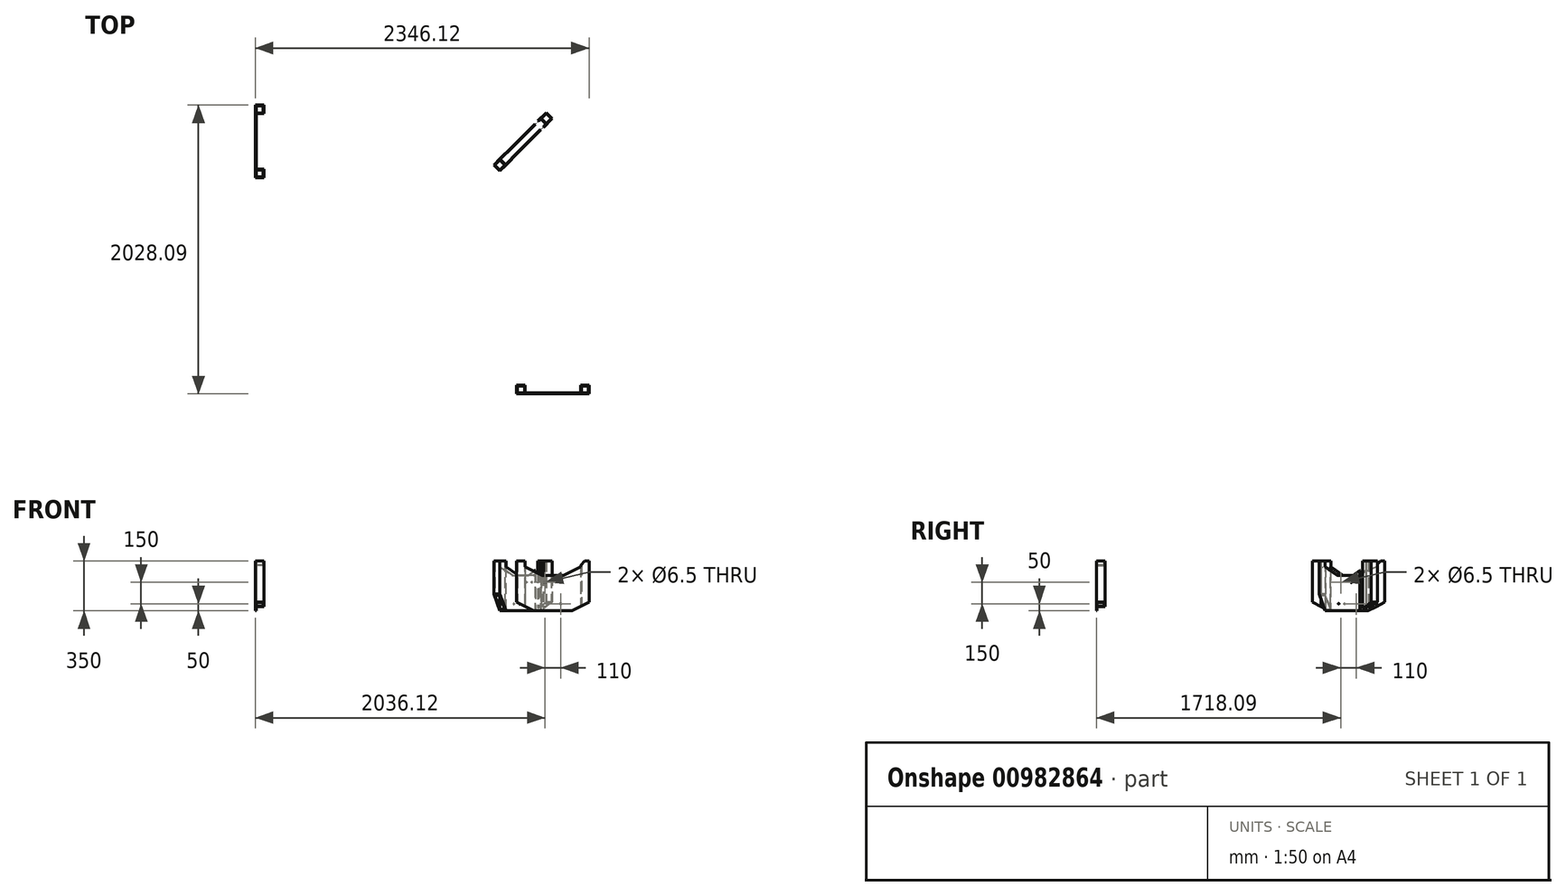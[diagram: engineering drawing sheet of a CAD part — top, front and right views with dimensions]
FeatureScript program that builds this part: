
annotation { "Feature Type Name" : "Feature", "Feature Type Description" : "" }
export const myFeature = defineFeature(function(context is Context, id is Id, definition is map)
    precondition{}
    {
        {
            var Q0;
            Q0=qCreatedBy(makeId("Top.planeOp"),FACE);
            var sketch = newSketch(context, id + "F0", { "sketchPlane" : qUnion([Q0])});
            skPoint(sketch, "E0.visualSharp", {"position": v(658.77, 766.57) * mm});
            skLineSegment(sketch, "E1.left", {"start": v(-1685.76, 286.57) * mm, "end": v(-1685.76, -13.43) * mm});
            skLineSegment(sketch, "E2.bottom", {"start": v(-1805.76, 536.57) * mm, "end": v(-1745.76, 536.57) * mm});
            skLineSegment(sketch, "E2.top", {"start": v(-1805.76, -163.43) * mm, "end": v(-1745.76, -163.43) * mm});
            skLineSegment(sketch, "E2.left", {"start": v(-1805.76, 536.57) * mm, "end": v(-1805.76, -163.43) * mm});
            skLineSegment(sketch, "E2.right", {"start": v(-1745.76, 536.57) * mm, "end": v(-1745.76, -163.43) * mm});
            skLineSegment(sketch, "E3", {"start": v(-1800.76, -163.43) * mm, "end": v(-1800.76, 536.57) * mm});
            skLineSegment(sketch, "E4", {"start": v(-1750.76, 536.57) * mm, "end": v(-1750.76, -163.43) * mm});
            skLineSegment(sketch, "E5.bottom", {"start": v(-64.64, -1586.52) * mm, "end": v(635.36, -1586.52) * mm});
            skLineSegment(sketch, "E5.top", {"start": v(-64.64, -1526.52) * mm, "end": v(635.36, -1526.52) * mm});
            skLineSegment(sketch, "E5.left", {"start": v(-64.64, -1586.52) * mm, "end": v(-64.64, -1526.52) * mm});
            skLineSegment(sketch, "E5.right", {"start": v(635.36, -1586.52) * mm, "end": v(635.36, -1526.52) * mm});
            skLineSegment(sketch, "E6", {"start": v(-64.64, -1531.52) * mm, "end": v(635.36, -1531.52) * mm});
            skLineSegment(sketch, "E7", {"start": v(635.36, -1581.52) * mm, "end": v(-64.64, -1581.52) * mm});
            skLineSegment(sketch, "E8.bottom", {"start": v(-1735.76, 581.57) * mm, "end": v(-1685.76, 581.57) * mm});
            skLineSegment(sketch, "E8.top", {"start": v(-1735.76, -208.43) * mm, "end": v(-1685.76, -208.43) * mm});
            skLineSegment(sketch, "E8.left", {"start": v(-1735.76, 581.57) * mm, "end": v(-1735.76, -208.43) * mm});
            skLineSegment(sketch, "E8.right", {"start": v(-1685.76, 581.57) * mm, "end": v(-1685.76, -208.43) * mm});
            skLineSegment(sketch, "E9.bottom", {"start": v(-1685.76, -208.43) * mm, "end": v(-460.76, -208.43) * mm});
            skLineSegment(sketch, "E9.top", {"start": v(-1685.76, -183.43) * mm, "end": v(-460.76, -183.43) * mm});
            skLineSegment(sketch, "E9.left", {"start": v(-1685.76, -208.43) * mm, "end": v(-1685.76, -183.43) * mm});
            skLineSegment(sketch, "E9.right", {"start": v(-460.76, -208.43) * mm, "end": v(-460.76, -183.43) * mm});
            skLineSegment(sketch, "E10.bottom", {"start": v(-1685.76, 581.57) * mm, "end": v(-460.76, 581.57) * mm});
            skLineSegment(sketch, "E10.top", {"start": v(-1685.76, 491.57) * mm, "end": v(-460.76, 491.57) * mm});
            skLineSegment(sketch, "E10.left", {"start": v(-1685.76, 581.57) * mm, "end": v(-1685.76, 491.57) * mm});
            skLineSegment(sketch, "E10.right", {"start": v(-460.76, 581.57) * mm, "end": v(-460.76, 491.57) * mm});
            skLineSegment(sketch, "E11", {"start": v(-341.23, -28.43) * mm, "end": v(-136.23, -28.43) * mm});
            skLineSegment(sketch, "E12", {"start": v(-136.23, -28.43) * mm, "end": v(-136.23, -233.43) * mm});
            skLineSegment(sketch, "E13", {"start": v(-341.23, -3.43) * mm, "end": v(-111.23, -3.43) * mm});
            skLineSegment(sketch, "E14", {"start": v(-111.23, -3.43) * mm, "end": v(-111.23, -233.43) * mm});
            skLineSegment(sketch, "E15.bottom", {"start": v(-520.76, 491.57) * mm, "end": v(-545.76, 491.57) * mm});
            skLineSegment(sketch, "E15.top", {"start": v(-520.76, -183.43) * mm, "end": v(-545.76, -183.43) * mm});
            skLineSegment(sketch, "E15.left", {"start": v(-520.76, 491.57) * mm, "end": v(-520.76, -183.43) * mm});
            skLineSegment(sketch, "E15.right", {"start": v(-545.76, 491.57) * mm, "end": v(-545.76, -183.43) * mm});
            skLineSegment(sketch, "E16.bottom", {"start": v(-291.23, -3.43) * mm, "end": v(-266.23, -3.43) * mm});
            skLineSegment(sketch, "E17.left", {"start": v(-111.23, -158.43) * mm, "end": v(-111.23, -183.43) * mm});
            skLineSegment(sketch, "E18", {"start": v(-109.64, -1491.52) * mm, "end": v(-109.64, -1516.52) * mm});
            skLineSegment(sketch, "E19", {"start": v(-109.64, -1516.52) * mm, "end": v(680.36, -1516.52) * mm});
            skLineSegment(sketch, "E20", {"start": v(680.36, -1516.52) * mm, "end": v(680.36, -1491.52) * mm});
            skLineSegment(sketch, "E21.top", {"start": v(-109.64, -391.52) * mm, "end": v(-84.64, -391.52) * mm});
            skLineSegment(sketch, "E21.left", {"start": v(-109.64, -1491.52) * mm, "end": v(-109.64, -391.52) * mm});
            skLineSegment(sketch, "E21.right", {"start": v(-84.64, -1491.52) * mm, "end": v(-84.64, -391.52) * mm});
            skLineSegment(sketch, "E22.top", {"start": v(680.36, -391.52) * mm, "end": v(590.36, -391.52) * mm});
            skLineSegment(sketch, "E22.left", {"start": v(680.36, -1491.52) * mm, "end": v(680.36, -391.52) * mm});
            skLineSegment(sketch, "E22.right", {"start": v(590.36, -1491.52) * mm, "end": v(590.36, -391.52) * mm});
            skLineSegment(sketch, "E23.bottom", {"start": v(-84.64, -441.52) * mm, "end": v(590.36, -441.52) * mm});
            skLineSegment(sketch, "E23.top", {"start": v(-84.64, -466.52) * mm, "end": v(590.36, -466.52) * mm});
            skLineSegment(sketch, "E23.left", {"start": v(-84.64, -441.52) * mm, "end": v(-84.64, -466.52) * mm});
            skLineSegment(sketch, "E23.right", {"start": v(590.36, -441.52) * mm, "end": v(590.36, -466.52) * mm});
            skLineSegment(sketch, "E24.top", {"start": v(-1745.76, 11.57) * mm, "end": v(-1735.76, 11.57) * mm});
            skLineSegment(sketch, "E24.left", {"start": v(-1745.76, 49.07) * mm, "end": v(-1745.76, 11.57) * mm});
            skLineSegment(sketch, "E24.right", {"start": v(-1735.76, 49.07) * mm, "end": v(-1735.76, 11.57) * mm});
            skLineSegment(sketch, "E25.left", {"start": v(-1745.76, 349.07) * mm, "end": v(-1745.76, 324.07) * mm});
            skLineSegment(sketch, "E25.right", {"start": v(-1735.76, 349.07) * mm, "end": v(-1735.76, 324.07) * mm});
            skLineSegment(sketch, "E26.bottom", {"start": v(110.36, -1526.52) * mm, "end": v(160.36, -1526.52) * mm});
            skLineSegment(sketch, "E26.top", {"start": v(110.36, -1516.52) * mm, "end": v(160.36, -1516.52) * mm});
            skLineSegment(sketch, "E26.left", {"start": v(110.36, -1526.52) * mm, "end": v(110.36, -1516.52) * mm});
            skLineSegment(sketch, "E26.right", {"start": v(160.36, -1526.52) * mm, "end": v(160.36, -1516.52) * mm});
            skLineSegment(sketch, "E27.bottom", {"start": v(410.36, -1526.52) * mm, "end": v(460.36, -1526.52) * mm});
            skLineSegment(sketch, "E27.top", {"start": v(410.36, -1516.52) * mm, "end": v(460.36, -1516.52) * mm});
            skLineSegment(sketch, "E27.left", {"start": v(410.36, -1526.52) * mm, "end": v(410.36, -1516.52) * mm});
            skLineSegment(sketch, "E27.right", {"start": v(460.36, -1526.52) * mm, "end": v(460.36, -1516.52) * mm});
            skLineSegment(sketch, "E28", {"start": v(-128.9, 14.25) * mm, "end": v(220.91, 364.07) * mm});
            skLineSegment(sketch, "E29", {"start": v(-93.55, -21.1) * mm, "end": v(256.27, 328.72) * mm});
            skLineSegment(sketch, "E30", {"start": v(256.27, 328.72) * mm, "end": v(273.95, 346.4) * mm});
            skLineSegment(sketch, "E31", {"start": v(220.91, 364.07) * mm, "end": v(238.6, 381.75) * mm});
            skLineSegment(sketch, "E32", {"start": v(238.6, 381.75) * mm, "end": v(273.95, 417.1) * mm});
            skLineSegment(sketch, "E33", {"start": v(309.3, 381.75) * mm, "end": v(273.95, 346.4) * mm});
            skLineSegment(sketch, "E34", {"start": v(309.3, 381.75) * mm, "end": v(380.01, 452.46) * mm});
            skLineSegment(sketch, "E35", {"start": v(380.01, 452.46) * mm, "end": v(344.66, 487.81) * mm});
            skLineSegment(sketch, "E36", {"start": v(344.66, 487.81) * mm, "end": v(273.95, 417.1) * mm});
            skLineSegment(sketch, "E37", {"start": v(380.01, 452.46) * mm, "end": v(383.55, 448.92) * mm});
            skLineSegment(sketch, "E38", {"start": v(383.55, 448.92) * mm, "end": v(-111.23, -45.86) * mm});
            skLineSegment(sketch, "E39", {"start": v(-93.55, -21.1) * mm, "end": v(-111.23, -38.78) * mm});
            skLineSegment(sketch, "E40", {"start": v(-128.9, 14.25) * mm, "end": v(-146.59, -3.43) * mm});
            skLineSegment(sketch, "E41", {"start": v(344.66, 487.81) * mm, "end": v(341.12, 491.35) * mm});
            skLineSegment(sketch, "E42", {"start": v(341.12, 491.35) * mm, "end": v(-153.66, -3.43) * mm});
            skLineSegment(sketch, "E43", {"start": v(247.43, 390.59) * mm, "end": v(282.78, 355.23) * mm});
            skLineSegment(sketch, "E44", {"start": v(-341.23, -28.43) * mm, "end": v(-341.23, -3.43) * mm});
            skLineSegment(sketch, "E45", {"start": v(-136.23, -233.43) * mm, "end": v(-111.23, -233.43) * mm});
            skLineSegment(sketch, "E46", {"start": v(-1745.76, 61.57) * mm, "end": v(-1735.76, 61.57) * mm});
            skLineSegment(sketch, "E47", {"start": v(-1745.76, 361.57) * mm, "end": v(-1735.76, 361.57) * mm});
            skLineSegment(sketch, "E48", {"start": v(-1745.76, 311.57) * mm, "end": v(-1735.76, 311.57) * mm});
            skLineSegment(sketch, "E49", {"start": v(590.36, -391.52) * mm, "end": v(-84.64, -391.52) * mm});
            skLineSegment(sketch, "E50", {"start": v(-111.23, -233.43) * mm, "end": v(603.77, -233.43) * mm});
            skLineSegment(sketch, "E51", {"start": v(-341.23, -3.43) * mm, "end": v(-341.23, 711.57) * mm});
            skLineSegment(sketch, "E52", {"start": v(-460.76, 491.57) * mm, "end": v(-460.76, -183.43) * mm});
            skLineSegment(sketch, "E53", {"start": v(-1260.76, -208.43) * mm, "end": v(-1260.76, 581.57) * mm});
            skLineSegment(sketch, "E54", {"start": v(-1235.76, 581.57) * mm, "end": v(-1235.76, -208.43) * mm});
            skLineSegment(sketch, "E55", {"start": v(-109.64, -1016.52) * mm, "end": v(680.36, -1016.52) * mm});
            skLineSegment(sketch, "E56", {"start": v(-109.64, -1041.52) * mm, "end": v(680.36, -1041.52) * mm});
            skLineSegment(sketch, "E57", {"start": v(-341.23, 711.57) * mm, "end": v(-341.23, 761.57) * mm});
            skLineSegment(sketch, "E58", {"start": v(603.77, -233.43) * mm, "end": v(653.77, -233.43) * mm});
            skLineSegment(sketch, "E59", {"start": v(282.78, 355.23) * mm, "end": v(653.77, -15.75) * mm});
            skLineSegment(sketch, "E60", {"start": v(653.77, -233.43) * mm, "end": v(653.77, -15.75) * mm});
            skLineSegment(sketch, "E61", {"start": v(247.43, 390.59) * mm, "end": v(-123.55, 761.57) * mm});
            skLineSegment(sketch, "E62", {"start": v(-341.23, 761.57) * mm, "end": v(-123.55, 761.57) * mm});
            skLineSegment(sketch, "E63", {"start": v(-111.23, -158.43) * mm, "end": v(603.77, -158.43) * mm});
            skLineSegment(sketch, "E64", {"start": v(-111.23, -183.43) * mm, "end": v(603.77, -183.43) * mm});
            skLineSegment(sketch, "E65", {"start": v(-291.23, -3.43) * mm, "end": v(-291.23, 711.57) * mm});
            skLineSegment(sketch, "E66", {"start": v(-266.23, -3.43) * mm, "end": v(-266.23, 711.57) * mm});
            skLineSegment(sketch, "E67.bottom", {"start": v(-341.23, 761.57) * mm, "end": v(-391.23, 761.57) * mm});
            skLineSegment(sketch, "E67.left", {"start": v(-341.23, 761.57) * mm, "end": v(-341.23, 711.57) * mm});
            skLineSegment(sketch, "E68.bottom", {"start": v(-341.23, -3.43) * mm, "end": v(-391.23, -3.43) * mm});
            skLineSegment(sketch, "E68.top", {"start": v(-341.23, -28.43) * mm, "end": v(-391.23, -28.43) * mm});
            skLineSegment(sketch, "E68.left", {"start": v(-341.23, -3.43) * mm, "end": v(-341.23, -28.43) * mm});
            skLineSegment(sketch, "E68.right", {"start": v(-391.23, -3.43) * mm, "end": v(-391.23, -28.43) * mm});
            skLineSegment(sketch, "E69.bottom", {"start": v(-111.23, -233.43) * mm, "end": v(-136.23, -233.43) * mm});
            skLineSegment(sketch, "E69.top", {"start": v(-111.23, -283.43) * mm, "end": v(-136.23, -283.43) * mm});
            skLineSegment(sketch, "E69.left", {"start": v(-111.23, -233.43) * mm, "end": v(-111.23, -283.43) * mm});
            skLineSegment(sketch, "E69.right", {"start": v(-136.23, -233.43) * mm, "end": v(-136.23, -283.43) * mm});
            skLineSegment(sketch, "E70.right", {"start": v(653.77, -233.43) * mm, "end": v(653.77, -283.43) * mm});
            skLineSegment(sketch, "E71", {"start": v(-1800.76, -13.43) * mm, "end": v(-1750.76, -13.43) * mm});
            skLineSegment(sketch, "E72", {"start": v(-1800.76, -63.43) * mm, "end": v(-1750.76, -63.43) * mm});
            skLineSegment(sketch, "E73.bottom", {"start": v(-1795.76, -18.43) * mm, "end": v(-1755.76, -18.43) * mm});
            skLineSegment(sketch, "E73.top", {"start": v(-1795.76, -58.43) * mm, "end": v(-1755.76, -58.43) * mm});
            skLineSegment(sketch, "E73.left", {"start": v(-1795.76, -18.43) * mm, "end": v(-1795.76, -58.43) * mm});
            skLineSegment(sketch, "E73.right", {"start": v(-1755.76, -18.43) * mm, "end": v(-1755.76, -58.43) * mm});
            skLineSegment(sketch, "E74", {"start": v(35.36, -1581.52) * mm, "end": v(35.36, -1531.52) * mm});
            skLineSegment(sketch, "E75", {"start": v(85.36, -1581.52) * mm, "end": v(85.36, -1531.52) * mm});
            skLineSegment(sketch, "E76.bottom", {"start": v(40.36, -1536.52) * mm, "end": v(80.36, -1536.52) * mm});
            skLineSegment(sketch, "E76.top", {"start": v(40.36, -1576.52) * mm, "end": v(80.36, -1576.52) * mm});
            skLineSegment(sketch, "E76.left", {"start": v(40.36, -1536.52) * mm, "end": v(40.36, -1576.52) * mm});
            skLineSegment(sketch, "E76.right", {"start": v(80.36, -1536.52) * mm, "end": v(80.36, -1576.52) * mm});
            skLineSegment(sketch, "E77", {"start": v(238.6, 311.04) * mm, "end": v(203.24, 346.4) * mm});
            skLineSegment(sketch, "E78", {"start": v(273.95, 346.4) * mm, "end": v(238.6, 381.75) * mm});
            skLineSegment(sketch, "E79", {"start": v(210.34, 346.36) * mm, "end": v(238.62, 374.65) * mm});
            skLineSegment(sketch, "E80", {"start": v(238.62, 374.65) * mm, "end": v(266.9, 346.36) * mm});
            skLineSegment(sketch, "E81", {"start": v(266.9, 346.36) * mm, "end": v(238.62, 318.08) * mm});
            skLineSegment(sketch, "E82", {"start": v(238.62, 318.08) * mm, "end": v(210.34, 346.36) * mm});
            skLineSegment(sketch, "E83", {"start": v(-109.64, -1466.52) * mm, "end": v(680.36, -1466.52) * mm});
            skLineSegment(sketch, "E84", {"start": v(-1685.76, 486.57) * mm, "end": v(-460.76, 486.57) * mm});
            skLineSegment(sketch, "E85", {"start": v(-460.76, 581.57) * mm, "end": v(-460.76, 586.57) * mm});
            skLineSegment(sketch, "E86", {"start": v(-1735.76, 581.57) * mm, "end": v(-1735.76, 586.57) * mm});
            skLineSegment(sketch, "E87", {"start": v(-1735.76, 586.57) * mm, "end": v(-460.76, 586.57) * mm});
            skLineSegment(sketch, "E88", {"start": v(-1685.76, 581.57) * mm, "end": v(-1685.76, 586.57) * mm});
            skLineSegment(sketch, "E89", {"start": v(680.36, -391.52) * mm, "end": v(685.36, -391.52) * mm});
            skLineSegment(sketch, "E90", {"start": v(680.36, -1516.52) * mm, "end": v(685.36, -1516.52) * mm});
            skLineSegment(sketch, "E91", {"start": v(680.36, -1466.52) * mm, "end": v(685.36, -1466.52) * mm});
            skLineSegment(sketch, "E92", {"start": v(685.36, -1516.52) * mm, "end": v(685.36, -391.52) * mm});
            skLineSegment(sketch, "E93", {"start": v(585.36, -391.52) * mm, "end": v(585.36, -1466.52) * mm});
            skLineSegment(sketch, "E94.bottom", {"start": v(-1217.06, 852.71) * mm, "end": v(-592.06, 852.71) * mm});
            skLineSegment(sketch, "E94.top", {"start": v(-1217.06, 752.71) * mm, "end": v(-592.06, 752.71) * mm});
            skLineSegment(sketch, "E94.left", {"start": v(-1217.06, 852.71) * mm, "end": v(-1217.06, 752.71) * mm});
            skLineSegment(sketch, "E94.right", {"start": v(-592.06, 852.71) * mm, "end": v(-592.06, 752.71) * mm});
            skLineSegment(sketch, "E95.bottom", {"start": v(943.97, -569.98) * mm, "end": v(1043.97, -569.98) * mm});
            skLineSegment(sketch, "E95.top", {"start": v(943.97, -1344.98) * mm, "end": v(1043.97, -1344.98) * mm});
            skLineSegment(sketch, "E95.left", {"start": v(943.97, -569.98) * mm, "end": v(943.97, -1344.98) * mm});
            skLineSegment(sketch, "E95.right", {"start": v(1043.97, -569.98) * mm, "end": v(1043.97, -1344.98) * mm});
            skLineSegment(sketch, "E96", {"start": v(653.77, -283.43) * mm, "end": v(658.77, -283.43) * mm});
            skLineSegment(sketch, "E97", {"start": v(286.32, 351.7) * mm, "end": v(289.86, 355.23) * mm});
            skLineSegment(sketch, "E98", {"start": v(289.86, 355.23) * mm, "end": v(658.77, -13.68) * mm});
            skLineSegment(sketch, "E99", {"start": v(658.77, -13.68) * mm, "end": v(658.77, -283.43) * mm});
            skLineSegment(sketch, "E100", {"start": v(-391.23, 761.57) * mm, "end": v(-391.23, 766.57) * mm});
            skLineSegment(sketch, "E101", {"start": v(-391.23, 766.57) * mm, "end": v(-121.48, 766.57) * mm});
            skLineSegment(sketch, "E102", {"start": v(-121.48, 766.57) * mm, "end": v(289.86, 355.23) * mm});
            skLineSegment(sketch, "E103", {"start": v(-391.23, 761.57) * mm, "end": v(-391.23, 671.57) * mm});
            skLineSegment(sketch, "E104", {"start": v(-391.23, 671.57) * mm, "end": v(-391.23, 666.57) * mm});
            skLineSegment(sketch, "E105", {"start": v(653.77, -283.43) * mm, "end": v(563.77, -283.43) * mm});
            skLineSegment(sketch, "E106", {"start": v(563.77, -283.43) * mm, "end": v(558.77, -283.43) * mm});
            skLineSegment(sketch, "E107", {"start": v(286.32, 351.7) * mm, "end": v(222.68, 288.06) * mm});
            skLineSegment(sketch, "E108", {"start": v(563.77, -283.43) * mm, "end": v(563.77, -53.03) * mm});
            skLineSegment(sketch, "E109", {"start": v(-391.23, 671.57) * mm, "end": v(-160.83, 671.57) * mm});
            skLineSegment(sketch, "E110", {"start": v(-160.83, 671.57) * mm, "end": v(563.77, -53.03) * mm});
            skLineSegment(sketch, "E111", {"start": v(180.25, 330.48) * mm, "end": v(176.72, 326.95) * mm});
            skLineSegment(sketch, "E112", {"start": v(176.72, 326.95) * mm, "end": v(-162.9, 666.57) * mm});
            skLineSegment(sketch, "E113", {"start": v(-162.9, 666.57) * mm, "end": v(-391.23, 666.57) * mm});
            skLineSegment(sketch, "E114", {"start": v(176.72, 326.95) * mm, "end": v(558.77, -55.1) * mm});
            skLineSegment(sketch, "E115", {"start": v(558.77, -55.1) * mm, "end": v(558.77, -283.43) * mm});
            skLineSegment(sketch, "E116", {"start": v(466.78, 1211.56) * mm, "end": v(466.78, 1216.56) * mm});
            skLineSegment(sketch, "E117", {"start": v(466.78, 1216.56) * mm, "end": v(736.53, 1216.56) * mm});
            skLineSegment(sketch, "E118", {"start": v(466.78, 1211.56) * mm, "end": v(466.78, 1121.56) * mm});
            skLineSegment(sketch, "E119", {"start": v(466.78, 1121.56) * mm, "end": v(466.78, 1116.56) * mm});
            skLineSegment(sketch, "E120", {"start": v(1034.73, 776.93) * mm, "end": v(695.11, 1116.56) * mm});
            skLineSegment(sketch, "E121", {"start": v(695.11, 1116.56) * mm, "end": v(466.78, 1116.56) * mm});
            skLineSegment(sketch, "E122", {"start": v(736.53, 1216.56) * mm, "end": v(1105.44, 847.64) * mm});
            skLineSegment(sketch, "E123", {"start": v(1034.73, 776.93) * mm, "end": v(1105.44, 847.64) * mm});
            skLineSegment(sketch, "E124", {"start": v(1556.93, 75.78) * mm, "end": v(1561.93, 75.78) * mm});
            skLineSegment(sketch, "E125", {"start": v(1193.02, 714.44) * mm, "end": v(1561.93, 345.53) * mm});
            skLineSegment(sketch, "E126", {"start": v(1561.93, 345.53) * mm, "end": v(1561.93, 75.78) * mm});
            skLineSegment(sketch, "E127", {"start": v(1556.93, 75.78) * mm, "end": v(1466.93, 75.78) * mm});
            skLineSegment(sketch, "E128", {"start": v(1466.93, 75.78) * mm, "end": v(1461.93, 75.78) * mm});
            skLineSegment(sketch, "E129", {"start": v(1461.93, 304.1) * mm, "end": v(1461.93, 75.78) * mm});
            skLineSegment(sketch, "E130", {"start": v(1461.93, 304.1) * mm, "end": v(1122.3, 643.73) * mm});
            skLineSegment(sketch, "E131", {"start": v(1193.02, 714.44) * mm, "end": v(1122.3, 643.73) * mm});
            skLineSegment(sketch, "E132", {"start": v(653.77, -15.75) * mm, "end": v(658.77, -13.68) * mm});
            skLineSegment(sketch, "E133", {"start": v(-123.55, 761.57) * mm, "end": v(-121.48, 766.57) * mm});
            skLineSegment(sketch, "E134", {"start": v(-311.2, 1156.99) * mm, "end": v(-93.53, 1156.99) * mm});
            skLineSegment(sketch, "E135.bottom", {"start": v(-311.2, 1156.99) * mm, "end": v(-361.2, 1156.99) * mm});
            skLineSegment(sketch, "E136", {"start": v(-361.2, 1156.99) * mm, "end": v(-361.2, 1161.99) * mm});
            skLineSegment(sketch, "E137", {"start": v(-361.2, 1161.99) * mm, "end": v(-91.46, 1161.99) * mm});
            skLineSegment(sketch, "E138", {"start": v(-93.53, 1156.99) * mm, "end": v(-91.46, 1161.99) * mm});
            skLineSegment(sketch, "E139", {"start": v(155.13, 973.03) * mm, "end": v(157.2, 978.03) * mm});
            skLineSegment(sketch, "E140", {"start": v(155.13, 973.03) * mm, "end": v(522.58, 605.58) * mm});
            skLineSegment(sketch, "E141", {"start": v(157.2, 978.03) * mm, "end": v(526.12, 609.11) * mm});
            skLineSegment(sketch, "E142", {"start": v(526.12, 609.11) * mm, "end": v(522.58, 605.58) * mm});
            skLineSegment(sketch, "E143", {"start": v(800.2, -243.65) * mm, "end": v(800.2, -25.98) * mm});
            skLineSegment(sketch, "E144.right", {"start": v(800.2, -243.65) * mm, "end": v(800.2, -293.65) * mm});
            skLineSegment(sketch, "E145", {"start": v(800.2, -293.65) * mm, "end": v(805.2, -293.65) * mm});
            skLineSegment(sketch, "E146", {"start": v(805.2, -23.9) * mm, "end": v(805.2, -293.65) * mm});
            skLineSegment(sketch, "E147", {"start": v(800.2, -25.98) * mm, "end": v(805.2, -23.9) * mm});
            skLineSegment(sketch, "E148", {"start": v(587.67, 634.51) * mm, "end": v(956.58, 265.6) * mm});
            skLineSegment(sketch, "E149", {"start": v(951.58, 263.53) * mm, "end": v(956.58, 265.6) * mm});
            skLineSegment(sketch, "E150", {"start": v(587.67, 634.51) * mm, "end": v(584.13, 630.98) * mm});
            skLineSegment(sketch, "E151", {"start": v(584.13, 630.98) * mm, "end": v(951.58, 263.53) * mm});
            skLineSegment(sketch, "E152.bottom", {"start": v(1162.31, -284.11) * mm, "end": v(1167.31, -284.11) * mm});
            skLineSegment(sketch, "E152.top", {"start": v(1162.31, -1359.11) * mm, "end": v(1167.31, -1359.11) * mm});
            skLineSegment(sketch, "E152.left", {"start": v(1162.31, -284.11) * mm, "end": v(1162.31, -1359.11) * mm});
            skLineSegment(sketch, "E152.right", {"start": v(1167.31, -284.11) * mm, "end": v(1167.31, -1359.11) * mm});
            skLineSegment(sketch, "E153.bottom", {"start": v(-1710.19, 1266.2) * mm, "end": v(-485.19, 1266.2) * mm});
            skLineSegment(sketch, "E153.top", {"start": v(-1710.19, 1261.2) * mm, "end": v(-485.19, 1261.2) * mm});
            skLineSegment(sketch, "E153.left", {"start": v(-1710.19, 1266.2) * mm, "end": v(-1710.19, 1261.2) * mm});
            skLineSegment(sketch, "E153.right", {"start": v(-485.19, 1266.2) * mm, "end": v(-485.19, 1261.2) * mm});
            skLineSegment(sketch, "E154", {"start": v(-1235.76, 461.57) * mm, "end": v(-460.76, 461.57) * mm});
            skLineSegment(sketch, "E155", {"start": v(560.36, -1016.52) * mm, "end": v(560.36, -391.52) * mm});
            skLineSegment(sketch, "E156", {"start": v(558.77, -283.43) * mm, "end": v(533.77, -283.43) * mm});
            skLineSegment(sketch, "E157", {"start": v(-391.23, 666.57) * mm, "end": v(-391.23, 641.57) * mm});
            skLineSegment(sketch, "E158", {"start": v(176.72, 326.95) * mm, "end": v(159.04, 309.27) * mm});
            skLineSegment(sketch, "E159", {"start": v(159.04, 309.27) * mm, "end": v(-173.26, 641.57) * mm});
            skLineSegment(sketch, "E160", {"start": v(219.15, 284.52) * mm, "end": v(201.47, 266.84) * mm});
            skLineSegment(sketch, "E161", {"start": v(201.47, 266.84) * mm, "end": v(159.04, 309.27) * mm});
            skLineSegment(sketch, "E162", {"start": v(201.47, 266.84) * mm, "end": v(533.77, -65.46) * mm});
            skLineSegment(sketch, "E163", {"start": v(-391.23, 641.57) * mm, "end": v(-173.26, 641.57) * mm});
            skLineSegment(sketch, "E164", {"start": v(533.77, -65.46) * mm, "end": v(533.77, -283.43) * mm});
            skLineSegment(sketch, "E165.bottom", {"start": v(-520.76, 41.57) * mm, "end": v(-460.76, 41.57) * mm});
            skLineSegment(sketch, "E165.top", {"start": v(-520.76, 16.57) * mm, "end": v(-460.76, 16.57) * mm});
            skLineSegment(sketch, "E165.left", {"start": v(-520.76, 41.57) * mm, "end": v(-520.76, 16.57) * mm});
            skLineSegment(sketch, "E165.right", {"start": v(-460.76, 41.57) * mm, "end": v(-460.76, 16.57) * mm});
            skLineSegment(sketch, "E166.bottom", {"start": v(-520.76, 261.57) * mm, "end": v(-460.76, 261.57) * mm});
            skLineSegment(sketch, "E166.top", {"start": v(-520.76, 236.57) * mm, "end": v(-460.76, 236.57) * mm});
            skLineSegment(sketch, "E166.left", {"start": v(-520.76, 261.57) * mm, "end": v(-520.76, 236.57) * mm});
            skLineSegment(sketch, "E166.right", {"start": v(-460.76, 261.57) * mm, "end": v(-460.76, 236.57) * mm});
            skLineSegment(sketch, "E167", {"start": v(-391.23, 641.57) * mm, "end": v(-391.23, -3.43) * mm});
            skLineSegment(sketch, "E168", {"start": v(-291.23, -3.43) * mm, "end": v(-291.23, 196.57) * mm});
            skLineSegment(sketch, "E169", {"start": v(-291.23, 196.57) * mm, "end": v(-391.23, 196.57) * mm});
            skLineSegment(sketch, "E170", {"start": v(-391.23, 196.57) * mm, "end": v(-391.23, 221.57) * mm});
            skLineSegment(sketch, "E171", {"start": v(-391.23, 221.57) * mm, "end": v(-291.23, 221.57) * mm});
            skLineSegment(sketch, "E172", {"start": v(-291.23, 641.57) * mm, "end": v(-291.23, 441.57) * mm});
            skLineSegment(sketch, "E173", {"start": v(-291.23, 441.57) * mm, "end": v(-391.23, 441.57) * mm});
            skLineSegment(sketch, "E174", {"start": v(-391.23, 441.57) * mm, "end": v(-391.23, 416.57) * mm});
            skLineSegment(sketch, "E175", {"start": v(-391.23, 416.57) * mm, "end": v(-291.23, 416.57) * mm});
            skLineSegment(sketch, "E176", {"start": v(533.77, -183.43) * mm, "end": v(333.77, -183.43) * mm});
            skLineSegment(sketch, "E177", {"start": v(333.77, -183.43) * mm, "end": v(333.77, -283.43) * mm});
            skLineSegment(sketch, "E178", {"start": v(333.77, -283.43) * mm, "end": v(308.77, -283.43) * mm});
            skLineSegment(sketch, "E179", {"start": v(308.77, -283.43) * mm, "end": v(308.77, -183.43) * mm});
            skLineSegment(sketch, "E180", {"start": v(-111.23, -183.43) * mm, "end": v(88.77, -183.43) * mm});
            skLineSegment(sketch, "E181", {"start": v(88.77, -183.43) * mm, "end": v(88.77, -283.43) * mm});
            skLineSegment(sketch, "E182", {"start": v(88.77, -283.43) * mm, "end": v(113.77, -283.43) * mm});
            skLineSegment(sketch, "E183", {"start": v(113.77, -283.43) * mm, "end": v(113.77, -183.43) * mm});
            skLineSegment(sketch, "E184.bottom", {"start": v(115.36, -391.52) * mm, "end": v(140.36, -391.52) * mm});
            skLineSegment(sketch, "E184.top", {"start": v(115.36, -441.52) * mm, "end": v(140.36, -441.52) * mm});
            skLineSegment(sketch, "E184.left", {"start": v(115.36, -391.52) * mm, "end": v(115.36, -441.52) * mm});
            skLineSegment(sketch, "E184.right", {"start": v(140.36, -391.52) * mm, "end": v(140.36, -441.52) * mm});
            skLineSegment(sketch, "E185.bottom", {"start": v(335.36, -391.52) * mm, "end": v(360.36, -391.52) * mm});
            skLineSegment(sketch, "E185.top", {"start": v(335.36, -441.52) * mm, "end": v(360.36, -441.52) * mm});
            skLineSegment(sketch, "E185.left", {"start": v(335.36, -391.52) * mm, "end": v(335.36, -441.52) * mm});
            skLineSegment(sketch, "E185.right", {"start": v(360.36, -391.52) * mm, "end": v(360.36, -441.52) * mm});
            skLineSegment(sketch, "E186", {"start": v(485.36, -1581.52) * mm, "end": v(485.36, -1531.52) * mm});
            skLineSegment(sketch, "E187", {"start": v(535.36, -1581.52) * mm, "end": v(535.36, -1531.52) * mm});
            skLineSegment(sketch, "E188.bottom", {"start": v(490.36, -1536.52) * mm, "end": v(530.36, -1536.52) * mm});
            skLineSegment(sketch, "E188.top", {"start": v(490.36, -1576.52) * mm, "end": v(530.36, -1576.52) * mm});
            skLineSegment(sketch, "E188.left", {"start": v(490.36, -1536.52) * mm, "end": v(490.36, -1576.52) * mm});
            skLineSegment(sketch, "E188.right", {"start": v(530.36, -1536.52) * mm, "end": v(530.36, -1576.52) * mm});
            skLineSegment(sketch, "E189", {"start": v(-1800.76, 436.57) * mm, "end": v(-1750.76, 436.57) * mm});
            skLineSegment(sketch, "E190", {"start": v(-1800.76, 386.57) * mm, "end": v(-1750.76, 386.57) * mm});
            skLineSegment(sketch, "E191.bottom", {"start": v(-1795.76, 431.57) * mm, "end": v(-1755.76, 431.57) * mm});
            skLineSegment(sketch, "E191.top", {"start": v(-1795.76, 391.57) * mm, "end": v(-1755.76, 391.57) * mm});
            skLineSegment(sketch, "E191.left", {"start": v(-1795.76, 431.57) * mm, "end": v(-1795.76, 391.57) * mm});
            skLineSegment(sketch, "E191.right", {"start": v(-1755.76, 431.57) * mm, "end": v(-1755.76, 391.57) * mm});
            skLineSegment(sketch, "E192", {"start": v(-86.68, -14.23) * mm, "end": v(-122.03, 21.12) * mm});
            skLineSegment(sketch, "E193", {"start": v(-51.32, 21.12) * mm, "end": v(-86.68, 56.48) * mm});
            skLineSegment(sketch, "E194", {"start": v(-114.93, 21.1) * mm, "end": v(-86.65, 49.38) * mm});
            skLineSegment(sketch, "E195", {"start": v(-58.36, 21.1) * mm, "end": v(-86.65, -7.2) * mm});
            skLineSegment(sketch, "E196", {"start": v(-86.65, -7.2) * mm, "end": v(-114.93, 21.1) * mm});
            skLineSegment(sketch, "E197", {"start": v(-122.03, 21.12) * mm, "end": v(-125.57, 24.66) * mm});
            skLineSegment(sketch, "E198", {"start": v(-86.68, -14.23) * mm, "end": v(-83.14, -17.77) * mm});
            skLineSegment(sketch, "E199", {"start": v(238.6, 381.75) * mm, "end": v(235.06, 385.28) * mm});
            skLineSegment(sketch, "E200", {"start": v(273.95, 346.4) * mm, "end": v(277.48, 342.86) * mm});
            skLineSegment(sketch, "E201", {"start": v(281.02, 346.4) * mm, "end": v(238.6, 388.82) * mm});
            skLineSegment(sketch, "E202", {"start": v(-86.68, -21.3) * mm, "end": v(-129.1, 21.12) * mm});
            skLineSegment(sketch, "E203", {"start": v(-1800.76, -63.43) * mm, "end": v(-1805.76, -63.43) * mm});
            skLineSegment(sketch, "E204", {"start": v(-1750.76, -63.43) * mm, "end": v(-1745.76, -63.43) * mm});
            skLineSegment(sketch, "E205", {"start": v(-1745.76, -68.43) * mm, "end": v(-1805.76, -68.43) * mm});
            skLineSegment(sketch, "E206", {"start": v(-1745.76, 441.57) * mm, "end": v(-1805.76, 441.57) * mm});
            skLineSegment(sketch, "E207", {"start": v(30.36, -1586.52) * mm, "end": v(30.36, -1526.52) * mm});
            skLineSegment(sketch, "E208", {"start": v(540.36, -1586.52) * mm, "end": v(540.36, -1526.52) * mm});
            skCircle(sketch, "E209", {"center": v(-444.78, -697.98) * mm, "radius": 3.25 * mm});
            skLineSegment(sketch, "E210", {"start": v(-1805.76, -8.43) * mm, "end": v(-1745.76, -8.43) * mm});
            skLineSegment(sketch, "E211", {"start": v(-1805.76, 381.57) * mm, "end": v(-1745.76, 381.57) * mm});
            skLineSegment(sketch, "E212", {"start": v(-86.68, 63.55) * mm, "end": v(-44.25, 21.12) * mm});
            skLineSegment(sketch, "E213", {"start": v(238.6, 303.97) * mm, "end": v(196.16, 346.4) * mm});
            skLineSegment(sketch, "E214", {"start": v(90.36, -1526.52) * mm, "end": v(90.36, -1586.52) * mm});
            skLineSegment(sketch, "E215", {"start": v(480.36, -1586.52) * mm, "end": v(480.36, -1526.52) * mm});
            skSolve(sketch);
        }
        {
            var Q0;
            {var subQ1=sQuery(id+"F0.wireOp",EDGE,"E26.bottom");Q0=makeQuery(id+"F0.imprint","IMPRINT",FACE,{"disambiguationData":[TD([[makeQuery(id+"F0.imprint","IMPRINT",EDGE,{"derivedFrom":subQ1}),-1.0]])]});}
            var Q1;
            {var subQ0=sQuery(id+"F0.wireOp",EDGE,"E114");var subQ1=sQuery(id+"F0.wireOp",EDGE,"E29");var subQ2=makeQuery(id+"F0.imprint","INTERSECT",VERTEX,{"derivedFrom":[subQ1,subQ0]});Q1=makeQuery(id+"F0.imprint","IMPRINT",FACE,{"disambiguationData":[TD([[makeQuery(id+"F0.imprint","IMPRINT",EDGE,{"disambiguationData":[TD([[subQ2,-1.0]])],"derivedFrom":subQ1}),-1.0]])]});}
            var Q2;
            {var subQ5=sQuery(id+"F0.wireOp",EDGE,"E160");Q2=makeQuery(id+"F0.imprint","IMPRINT",FACE,{"disambiguationData":[TD([[makeQuery(id+"F0.imprint","IMPRINT",EDGE,{"derivedFrom":subQ5}),-1.0]])]});}
            var Q3;
            {var subQ5=sQuery(id+"F0.wireOp",EDGE,"E158");Q3=makeQuery(id+"F0.imprint","IMPRINT",FACE,{"disambiguationData":[TD([[makeQuery(id+"F0.imprint","IMPRINT",EDGE,{"derivedFrom":subQ5}),1.0]])]});}
            var Q4;
            {var subQ5=sQuery(id+"F0.wireOp",EDGE,"E111");Q4=makeQuery(id+"F0.imprint","IMPRINT",FACE,{"disambiguationData":[TD([[makeQuery(id+"F0.imprint","IMPRINT",EDGE,{"derivedFrom":subQ5}),1.0]])]});}
            var Q5;
            {var subQ7=sQuery(id+"F0.wireOp",EDGE,"E24.left");Q5=makeQuery(id+"F0.imprint","IMPRINT",FACE,{"disambiguationData":[TD([[makeQuery(id+"F0.imprint","IMPRINT",EDGE,{"derivedFrom":subQ7}),-1.0]])]});}
            var Q6;
            {var subQ0=sQuery(id+"F0.wireOp",EDGE,"E214");var subQ1=sQuery(id+"F0.wireOp",EDGE,"E5.bottom");var subQ2=makeQuery(id+"F0.imprint","INTERSECT",VERTEX,{"derivedFrom":[subQ1,subQ0]});Q6=makeQuery(id+"F0.imprint","IMPRINT",FACE,{"disambiguationData":[TD([[makeQuery(id+"F0.imprint","IMPRINT",EDGE,{"disambiguationData":[TD([[subQ2,-1.0]])],"derivedFrom":subQ1}),1.0]])]});}
            var Q7;
            {var subQ0=sQuery(id+"F0.wireOp",EDGE,"E212");var subQ1=sQuery(id+"F0.wireOp",EDGE,"E29");var subQ2=makeQuery(id+"F0.imprint","INTERSECT",VERTEX,{"derivedFrom":[subQ1,subQ0]});Q7=makeQuery(id+"F0.imprint","IMPRINT",FACE,{"disambiguationData":[TD([[makeQuery(id+"F0.imprint","IMPRINT",EDGE,{"disambiguationData":[TD([[subQ2,-1.0]])],"derivedFrom":subQ1}),-1.0]])]});}
            var Q8;
            {var subQ0=sQuery(id+"F0.wireOp",EDGE,"E212");var subQ1=sQuery(id+"F0.wireOp",EDGE,"E28");var subQ2=makeQuery(id+"F0.imprint","INTERSECT",VERTEX,{"derivedFrom":[subQ1,subQ0]});Q8=makeQuery(id+"F0.imprint","IMPRINT",FACE,{"disambiguationData":[TD([[makeQuery(id+"F0.imprint","IMPRINT",EDGE,{"disambiguationData":[TD([[subQ2,-1.0]])],"derivedFrom":subQ1}),1.0]])]});}
            var Q9;
            {var subQ0=sQuery(id+"F0.wireOp",EDGE,"E110");var subQ1=sQuery(id+"F0.wireOp",EDGE,"E28");var subQ2=makeQuery(id+"F0.imprint","INTERSECT",VERTEX,{"derivedFrom":[subQ1,subQ0]});Q9=makeQuery(id+"F0.imprint","IMPRINT",FACE,{"disambiguationData":[TD([[makeQuery(id+"F0.imprint","IMPRINT",EDGE,{"disambiguationData":[TD([[subQ2,-1.0]])],"derivedFrom":subQ1}),1.0]])]});}
            var Q10;
            {var subQ0=sQuery(id+"F0.wireOp",EDGE,"E110");var subQ1=sQuery(id+"F0.wireOp",EDGE,"E29");var subQ2=makeQuery(id+"F0.imprint","INTERSECT",VERTEX,{"derivedFrom":[subQ1,subQ0]});Q10=makeQuery(id+"F0.imprint","IMPRINT",FACE,{"disambiguationData":[TD([[makeQuery(id+"F0.imprint","IMPRINT",EDGE,{"disambiguationData":[TD([[subQ2,-1.0]])],"derivedFrom":subQ1}),-1.0]])]});}
            var Q11;
            {var subQ0=sQuery(id+"F0.wireOp",EDGE,"E210");var subQ1=sQuery(id+"F0.wireOp",EDGE,"E2.left");var subQ2=makeQuery(id+"F0.imprint","INTERSECT",VERTEX,{"derivedFrom":[subQ1,subQ0]});Q11=makeQuery(id+"F0.imprint","IMPRINT",FACE,{"disambiguationData":[TD([[makeQuery(id+"F0.imprint","IMPRINT",EDGE,{"disambiguationData":[TD([[subQ2,1.0]])],"derivedFrom":subQ1}),1.0]])]});}
            var Q12;
            {var subQ2=sQuery(id+"F0.wireOp",EDGE,"E206");var subQ5=sQuery(id+"F0.wireOp",EDGE,"E2.left");var subQ6=makeQuery(id+"F0.imprint","INTERSECT",VERTEX,{"derivedFrom":[subQ5,subQ2]});Q12=makeQuery(id+"F0.imprint","IMPRINT",FACE,{"disambiguationData":[TD([[makeQuery(id+"F0.imprint","IMPRINT",EDGE,{"disambiguationData":[TD([[subQ6,-1.0]])],"derivedFrom":subQ5}),1.0]])]});}
            var Q13;
            {var subQ0=sQuery(id+"F0.wireOp",EDGE,"E189");Q13=makeQuery(id+"F0.imprint","IMPRINT",FACE,{"disambiguationData":[TD([[makeQuery(id+"F0.imprint","IMPRINT",EDGE,{"derivedFrom":subQ0}),1.0]])]});}
            var Q14;
            {var subQ4=sQuery(id+"F0.wireOp",EDGE,"E206");var subQ5=sQuery(id+"F0.wireOp",EDGE,"E2.right");var subQ6=makeQuery(id+"F0.imprint","INTERSECT",VERTEX,{"derivedFrom":[subQ5,subQ4]});Q14=makeQuery(id+"F0.imprint","IMPRINT",FACE,{"disambiguationData":[TD([[makeQuery(id+"F0.imprint","IMPRINT",EDGE,{"disambiguationData":[TD([[subQ6,-1.0]])],"derivedFrom":subQ5}),-1.0]])]});}
            var Q15;
            {var subQ0=sQuery(id+"F0.wireOp",EDGE,"E190");Q15=makeQuery(id+"F0.imprint","IMPRINT",FACE,{"disambiguationData":[TD([[makeQuery(id+"F0.imprint","IMPRINT",EDGE,{"derivedFrom":subQ0}),-1.0]])]});}
            var Q16;
            {var subQ6=sQuery(id+"F0.wireOp",EDGE,"E203");Q16=makeQuery(id+"F0.imprint","IMPRINT",FACE,{"disambiguationData":[TD([[makeQuery(id+"F0.imprint","IMPRINT",EDGE,{"derivedFrom":subQ6}),-1.0]])]});}
            var Q17;
            {var subQ0=sQuery(id+"F0.wireOp",EDGE,"E71");Q17=makeQuery(id+"F0.imprint","IMPRINT",FACE,{"disambiguationData":[TD([[makeQuery(id+"F0.imprint","IMPRINT",EDGE,{"derivedFrom":subQ0}),1.0]])]});}
            var Q18;
            {var subQ2=sQuery(id+"F0.wireOp",EDGE,"E204");Q18=makeQuery(id+"F0.imprint","IMPRINT",FACE,{"disambiguationData":[TD([[makeQuery(id+"F0.imprint","IMPRINT",EDGE,{"derivedFrom":subQ2}),1.0]])]});}
            var Q19;
            {var subQ0=sQuery(id+"F0.wireOp",EDGE,"E204");Q19=makeQuery(id+"F0.imprint","IMPRINT",FACE,{"disambiguationData":[TD([[makeQuery(id+"F0.imprint","IMPRINT",EDGE,{"derivedFrom":subQ0}),-1.0]])]});}
            var Q20;
            {var subQ0=sQuery(id+"F0.wireOp",EDGE,"E72");Q20=makeQuery(id+"F0.imprint","IMPRINT",FACE,{"disambiguationData":[TD([[makeQuery(id+"F0.imprint","IMPRINT",EDGE,{"derivedFrom":subQ0}),-1.0]])]});}
            var Q21;
            {var subQ0=sQuery(id+"F0.wireOp",EDGE,"E203");Q21=makeQuery(id+"F0.imprint","IMPRINT",FACE,{"disambiguationData":[TD([[makeQuery(id+"F0.imprint","IMPRINT",EDGE,{"derivedFrom":subQ0}),1.0]])]});}
            var Q22;
            {var subQ0=sQuery(id+"F0.wireOp",EDGE,"E193");Q22=makeQuery(id+"F0.imprint","IMPRINT",FACE,{"disambiguationData":[TD([[makeQuery(id+"F0.imprint","IMPRINT",EDGE,{"derivedFrom":subQ0}),-1.0]])]});}
            var Q23;
            {var subQ0=sQuery(id+"F0.wireOp",EDGE,"E197");Q23=makeQuery(id+"F0.imprint","IMPRINT",FACE,{"disambiguationData":[TD([[makeQuery(id+"F0.imprint","IMPRINT",EDGE,{"derivedFrom":subQ0}),-1.0]])]});}
            var Q24;
            {var subQ0=sQuery(id+"F0.wireOp",EDGE,"E192");Q24=makeQuery(id+"F0.imprint","IMPRINT",FACE,{"disambiguationData":[TD([[makeQuery(id+"F0.imprint","IMPRINT",EDGE,{"derivedFrom":subQ0}),1.0]])]});}
            var Q25;
            {var subQ0=sQuery(id+"F0.wireOp",EDGE,"E197");Q25=makeQuery(id+"F0.imprint","IMPRINT",FACE,{"disambiguationData":[TD([[makeQuery(id+"F0.imprint","IMPRINT",EDGE,{"derivedFrom":subQ0}),1.0]])]});}
            var Q26;
            {var subQ0=sQuery(id+"F0.wireOp",EDGE,"E198");Q26=makeQuery(id+"F0.imprint","IMPRINT",FACE,{"disambiguationData":[TD([[makeQuery(id+"F0.imprint","IMPRINT",EDGE,{"derivedFrom":subQ0}),-1.0]])]});}
            var Q27;
            {var subQ0=sQuery(id+"F0.wireOp",EDGE,"E198");Q27=makeQuery(id+"F0.imprint","IMPRINT",FACE,{"disambiguationData":[TD([[makeQuery(id+"F0.imprint","IMPRINT",EDGE,{"derivedFrom":subQ0}),1.0]])]});}
            var Q28;
            {var subQ4=sQuery(id+"F0.wireOp",EDGE,"E31");Q28=makeQuery(id+"F0.imprint","IMPRINT",FACE,{"disambiguationData":[TD([[makeQuery(id+"F0.imprint","IMPRINT",EDGE,{"derivedFrom":subQ4}),1.0]])]});}
            var Q29;
            {var subQ0=sQuery(id+"F0.wireOp",EDGE,"E77");Q29=makeQuery(id+"F0.imprint","IMPRINT",FACE,{"disambiguationData":[TD([[makeQuery(id+"F0.imprint","IMPRINT",EDGE,{"derivedFrom":subQ0}),1.0]])]});}
            var Q30;
            {var subQ6=sQuery(id+"F0.wireOp",EDGE,"E30");Q30=makeQuery(id+"F0.imprint","IMPRINT",FACE,{"disambiguationData":[TD([[makeQuery(id+"F0.imprint","IMPRINT",EDGE,{"derivedFrom":subQ6}),-1.0]])]});}
            var Q31;
            {var subQ0=sQuery(id+"F0.wireOp",EDGE,"E200");Q31=makeQuery(id+"F0.imprint","IMPRINT",FACE,{"disambiguationData":[TD([[makeQuery(id+"F0.imprint","IMPRINT",EDGE,{"derivedFrom":subQ0}),1.0]])]});}
            var Q32;
            {var subQ0=sQuery(id+"F0.wireOp",EDGE,"E78");Q32=makeQuery(id+"F0.imprint","IMPRINT",FACE,{"disambiguationData":[TD([[makeQuery(id+"F0.imprint","IMPRINT",EDGE,{"derivedFrom":subQ0}),-1.0]])]});}
            var Q33;
            {var subQ0=sQuery(id+"F0.wireOp",EDGE,"E199");Q33=makeQuery(id+"F0.imprint","IMPRINT",FACE,{"disambiguationData":[TD([[makeQuery(id+"F0.imprint","IMPRINT",EDGE,{"derivedFrom":subQ0}),-1.0]])]});}
            var Q34;
            {var subQ0=sQuery(id+"F0.wireOp",EDGE,"E75");Q34=makeQuery(id+"F0.imprint","IMPRINT",FACE,{"disambiguationData":[TD([[makeQuery(id+"F0.imprint","IMPRINT",EDGE,{"derivedFrom":subQ0}),-1.0]])]});}
            var Q35;
            {var subQ3=sQuery(id+"F0.wireOp",EDGE,"E207");var subQ6=sQuery(id+"F0.wireOp",EDGE,"E5.top");var subQ9=makeQuery(id+"F0.imprint","INTERSECT",VERTEX,{"derivedFrom":[subQ6,subQ3]});Q35=makeQuery(id+"F0.imprint","IMPRINT",FACE,{"disambiguationData":[TD([[makeQuery(id+"F0.imprint","IMPRINT",EDGE,{"disambiguationData":[TD([[subQ9,-1.0]])],"derivedFrom":subQ6}),-1.0]])]});}
            var Q36;
            {var subQ0=sQuery(id+"F0.wireOp",EDGE,"E74");Q36=makeQuery(id+"F0.imprint","IMPRINT",FACE,{"disambiguationData":[TD([[makeQuery(id+"F0.imprint","IMPRINT",EDGE,{"derivedFrom":subQ0}),1.0]])]});}
            var Q37;
            {var subQ2=sQuery(id+"F0.wireOp",EDGE,"E207");var subQ4=sQuery(id+"F0.wireOp",EDGE,"E5.bottom");var subQ5=makeQuery(id+"F0.imprint","INTERSECT",VERTEX,{"derivedFrom":[subQ4,subQ2]});Q37=makeQuery(id+"F0.imprint","IMPRINT",FACE,{"disambiguationData":[TD([[makeQuery(id+"F0.imprint","IMPRINT",EDGE,{"disambiguationData":[TD([[subQ5,-1.0]])],"derivedFrom":subQ4}),1.0]])]});}
            var Q38;
            {var subQ5=sQuery(id+"F0.wireOp",EDGE,"E208");var subQ7=sQuery(id+"F0.wireOp",EDGE,"E5.bottom");var subQ8=makeQuery(id+"F0.imprint","INTERSECT",VERTEX,{"derivedFrom":[subQ7,subQ5]});Q38=makeQuery(id+"F0.imprint","IMPRINT",FACE,{"disambiguationData":[TD([[makeQuery(id+"F0.imprint","IMPRINT",EDGE,{"disambiguationData":[TD([[subQ8,1.0]])],"derivedFrom":subQ7}),1.0]])]});}
            var Q39;
            {var subQ0=sQuery(id+"F0.wireOp",EDGE,"E186");Q39=makeQuery(id+"F0.imprint","IMPRINT",FACE,{"disambiguationData":[TD([[makeQuery(id+"F0.imprint","IMPRINT",EDGE,{"derivedFrom":subQ0}),1.0]])]});}
            var Q40;
            {var subQ4=sQuery(id+"F0.wireOp",EDGE,"E5.top");var subQ7=sQuery(id+"F0.wireOp",EDGE,"E208");var subQ9=makeQuery(id+"F0.imprint","INTERSECT",VERTEX,{"derivedFrom":[subQ4,subQ7]});Q40=makeQuery(id+"F0.imprint","IMPRINT",FACE,{"disambiguationData":[TD([[makeQuery(id+"F0.imprint","IMPRINT",EDGE,{"disambiguationData":[TD([[subQ9,1.0]])],"derivedFrom":subQ4}),-1.0]])]});}
            var Q41;
            {var subQ0=sQuery(id+"F0.wireOp",EDGE,"E187");Q41=makeQuery(id+"F0.imprint","IMPRINT",FACE,{"disambiguationData":[TD([[makeQuery(id+"F0.imprint","IMPRINT",EDGE,{"derivedFrom":subQ0}),-1.0]])]});}
            extrude(context, id + "F1", {"entities" : qUnion([Q0, Q1, Q2, Q3, Q4, Q5, Q6, Q7, Q8, Q9, Q10, Q11, Q12, Q13, Q14, Q15, Q16, Q17, Q18, Q19, Q20, Q21, Q22, Q23, Q24, Q25, Q26, Q27, Q28, Q29, Q30, Q31, Q32, Q33, Q34, Q35, Q36, Q37, Q38, Q39, Q40, Q41]), "depth" : 350 * mm, "offsetDistance" : 25 * mm});
        }
        {
            var Q0;
            Q0=makeQuery(id+"F1.opExtrude","SWEPT_FACE",FACE,{"disambiguationData":[OSD([sQuery(id+"F0.wireOp",EDGE,"E38"),sQuery(id+"F0.wireOp",EDGE,"E107"),sQuery(id+"F0.wireOp",EDGE,"E160")])]});
            var sketch = newSketch(context, id + "F2", { "sketchPlane" : qUnion([Q0])});
            skCircle(sketch, "E216", {"center": v(243.65, 200) * mm, "radius": 3.25 * mm});
            skCircle(sketch, "E217", {"center": v(118.65, 50) * mm, "radius": 3.25 * mm});
            skLineSegment(sketch, "E218.bottom", {"start": v(-16.35, 350) * mm, "end": v(383.65, 350) * mm});
            skLineSegment(sketch, "E218.top", {"start": v(-16.35, 250) * mm, "end": v(383.65, 250) * mm});
            skLineSegment(sketch, "E218.left", {"start": v(-16.35, 350) * mm, "end": v(-16.35, 250) * mm});
            skLineSegment(sketch, "E218.right", {"start": v(383.65, 350) * mm, "end": v(383.65, 250) * mm});
            skLineSegment(sketch, "E219", {"start": v(-16.35, 310) * mm, "end": v(103.65, 250) * mm});
            skLineSegment(sketch, "E220", {"start": v(263.65, 250) * mm, "end": v(383.65, 310) * mm});
            skSolve(sketch);
        }
        {
            var Q0;
            Q0=makeQuery(id+"F2.imprint","IMPRINT",FACE,{"disambiguationData":[TD([[makeQuery(id+"F2.imprint","IMPRINT",EDGE,{"derivedFrom":sQuery(id+"F2.wireOp",EDGE,"E217")}),1.0]])]});
            var Q1;
            Q1=makeQuery(id+"F2.imprint","IMPRINT",FACE,{"disambiguationData":[TD([[makeQuery(id+"F2.imprint","IMPRINT",EDGE,{"derivedFrom":sQuery(id+"F2.wireOp",EDGE,"E216")}),1.0]])]});
            var Q2;
            Q2=makeQuery(id+"F2.imprint","IMPRINT",FACE,{"disambiguationData":[TD([[makeQuery(id+"F2.imprint","IMPRINT",EDGE,{"derivedFrom":sQuery(id+"F2.wireOp",EDGE,"E218.bottom")}),1.0]])]});
            extrude(context, id + "F3", {"entities" : qUnion([Q0, Q1, Q2]), "operationType" : NewBodyOperationType.REMOVE, "oppositeDirection" : true, "depth" : 100 * mm, "offsetDistance" : 25 * mm});
        }
        {
            var Q0;
            Q0=makeQuery(id+"F1.opExtrude","SWEPT_FACE",FACE,{"disambiguationData":[OSD([sQuery(id+"F0.wireOp",EDGE,"E2.right"),sQuery(id+"F0.wireOp",EDGE,"E24.left"),sQuery(id+"F0.wireOp",EDGE,"E25.left")])]});
            var sketch = newSketch(context, id + "F4", { "sketchPlane" : qUnion([Q0])});
            skCircle(sketch, "E221", {"center": v(131.57, 200) * mm, "radius": 3.25 * mm});
            skCircle(sketch, "E222", {"center": v(241.57, 50) * mm, "radius": 3.25 * mm});
            skLineSegment(sketch, "E223.bottom", {"start": v(381.57, 350) * mm, "end": v(-8.43, 350) * mm});
            skLineSegment(sketch, "E223.top", {"start": v(381.57, 250) * mm, "end": v(-8.43, 250) * mm});
            skLineSegment(sketch, "E223.left", {"start": v(381.57, 350) * mm, "end": v(381.57, 250) * mm});
            skLineSegment(sketch, "E223.right", {"start": v(-8.43, 350) * mm, "end": v(-8.43, 250) * mm});
            skLineSegment(sketch, "E224", {"start": v(381.57, 310) * mm, "end": v(261.57, 250) * mm});
            skLineSegment(sketch, "E225", {"start": v(111.57, 250) * mm, "end": v(-8.43, 310) * mm});
            skSolve(sketch);
        }
        {
            var Q0;
            Q0=makeQuery(id+"F4.imprint","IMPRINT",FACE,{"disambiguationData":[TD([[makeQuery(id+"F4.imprint","IMPRINT",EDGE,{"derivedFrom":sQuery(id+"F4.wireOp",EDGE,"E221")}),1.0]])]});
            var Q1;
            Q1=makeQuery(id+"F4.imprint","IMPRINT",FACE,{"disambiguationData":[TD([[makeQuery(id+"F4.imprint","IMPRINT",EDGE,{"derivedFrom":sQuery(id+"F4.wireOp",EDGE,"E222")}),1.0]])]});
            var Q2;
            Q2=makeQuery(id+"F4.imprint","IMPRINT",FACE,{"disambiguationData":[TD([[makeQuery(id+"F4.imprint","IMPRINT",EDGE,{"derivedFrom":sQuery(id+"F4.wireOp",EDGE,"E223.bottom")}),1.0]])]});
            extrude(context, id + "F5", {"entities" : qUnion([Q0, Q1, Q2]), "operationType" : NewBodyOperationType.REMOVE, "oppositeDirection" : true, "depth" : 100 * mm, "offsetDistance" : 25 * mm});
        }
        {
            var Q0;
            Q0=makeQuery(id+"F1.opExtrude","SWEPT_FACE",FACE,{"disambiguationData":[OSD([sQuery(id+"F0.wireOp",EDGE,"E5.bottom")])]});
            var sketch = newSketch(context, id + "F6", { "sketchPlane" : qUnion([Q0])});
            skCircle(sketch, "E226", {"center": v(230.36, 200) * mm, "radius": 3.25 * mm});
            skCircle(sketch, "E227", {"center": v(340.36, 50) * mm, "radius": 3.25 * mm});
            skLineSegment(sketch, "E228.bottom", {"start": v(90.36, 350) * mm, "end": v(480.36, 350) * mm});
            skLineSegment(sketch, "E228.top", {"start": v(90.36, 250) * mm, "end": v(480.36, 250) * mm});
            skLineSegment(sketch, "E228.left", {"start": v(90.36, 350) * mm, "end": v(90.36, 250) * mm});
            skLineSegment(sketch, "E228.right", {"start": v(480.36, 350) * mm, "end": v(480.36, 250) * mm});
            skLineSegment(sketch, "E229", {"start": v(360.36, 250) * mm, "end": v(480.36, 310) * mm});
            skLineSegment(sketch, "E230", {"start": v(90.36, 310) * mm, "end": v(210.36, 250) * mm});
            skSolve(sketch);
        }
        {
            var Q0;
            Q0=makeQuery(id+"F6.imprint","IMPRINT",FACE,{"disambiguationData":[TD([[makeQuery(id+"F6.imprint","IMPRINT",EDGE,{"derivedFrom":sQuery(id+"F6.wireOp",EDGE,"E226")}),1.0]])]});
            var Q1;
            Q1=makeQuery(id+"F6.imprint","IMPRINT",FACE,{"disambiguationData":[TD([[makeQuery(id+"F6.imprint","IMPRINT",EDGE,{"derivedFrom":sQuery(id+"F6.wireOp",EDGE,"E227")}),1.0]])]});
            var Q2;
            {var subQ1=sQuery(id+"F6.wireOp",EDGE,"E228.bottom");Q2=makeQuery(id+"F6.imprint","IMPRINT",FACE,{"disambiguationData":[TD([[makeQuery(id+"F6.imprint","IMPRINT",EDGE,{"derivedFrom":subQ1}),-1.0]])]});}
            extrude(context, id + "F7", {"entities" : qUnion([Q0, Q1, Q2]), "operationType" : NewBodyOperationType.REMOVE, "oppositeDirection" : true, "depth" : 100 * mm, "offsetDistance" : 25 * mm});
        }
        {
            var Q0;
            Q0=makeQuery(id+"F1.opExtrude","CAP_EDGE",EDGE,{"disambiguationData":[OSD([sQuery(id+"F0.wireOp",EDGE,"E206")])],"isStart":true});
            var Q1;
            Q1=makeQuery(id+"F1.opExtrude","CAP_EDGE",EDGE,{"disambiguationData":[OSD([sQuery(id+"F0.wireOp",EDGE,"E205")])],"isStart":true});
            var Q2;
            Q2=makeQuery(id+"F1.opExtrude","CAP_EDGE",EDGE,{"disambiguationData":[OSD([sQuery(id+"F0.wireOp",EDGE,"E208")])],"isStart":true});
            var Q3;
            Q3=makeQuery(id+"F1.opExtrude","CAP_EDGE",EDGE,{"disambiguationData":[OSD([sQuery(id+"F0.wireOp",EDGE,"E207")])],"isStart":true});
            var Q4;
            Q4=makeQuery(id+"F1.opExtrude","CAP_EDGE",EDGE,{"disambiguationData":[OSD([sQuery(id+"F0.wireOp",EDGE,"E201")])],"isStart":true});
            var Q5;
            Q5=makeQuery(id+"F1.opExtrude","CAP_EDGE",EDGE,{"disambiguationData":[OSD([sQuery(id+"F0.wireOp",EDGE,"E202")])],"isStart":true});
            chamfer(context, id + "F8", {"entities" : qUnion([Q0, Q1, Q2, Q3, Q4, Q5]), "chamferType" : ChamferType.TWO_OFFSETS, "width1" : 60 * mm, "oppositeDirection" : false, "width2" : 120 * mm, "tangentPropagation" : true});
        }
        {
            var Q0;
            Q0=makeQuery(id+"F3.boolean.opBoolean","MERGE",EDGE,{"derivedFrom":[makeQuery(id+"F1.opExtrude","CAP_EDGE",EDGE,{"disambiguationData":[OSD([sQuery(id+"F0.wireOp",EDGE,"E212")])],"isStart":false})],"fromTools":[makeQuery(id+"F3.opExtrude","SWEPT_EDGE",EDGE,{"disambiguationData":[OSD([sQuery(id+"F0.wireOp",EDGE,"E38"),sQuery(id+"F0.wireOp",EDGE,"E107"),sQuery(id+"F0.wireOp",EDGE,"E160"),sQuery(id+"F2.wireOp",EDGE,"E218.bottom"),sQuery(id+"F2.wireOp",EDGE,"E218.left")])]})]});
            var Q1;
            Q1=makeQuery(id+"F3.boolean.opBoolean","MERGE",EDGE,{"derivedFrom":[makeQuery(id+"F1.opExtrude","CAP_EDGE",EDGE,{"disambiguationData":[OSD([sQuery(id+"F0.wireOp",EDGE,"E213")])],"isStart":false})],"fromTools":[makeQuery(id+"F3.opExtrude","SWEPT_EDGE",EDGE,{"disambiguationData":[OSD([sQuery(id+"F0.wireOp",EDGE,"E38"),sQuery(id+"F0.wireOp",EDGE,"E107"),sQuery(id+"F0.wireOp",EDGE,"E160"),sQuery(id+"F2.wireOp",EDGE,"E218.bottom"),sQuery(id+"F2.wireOp",EDGE,"E218.right")])]})]});
            var Q2;
            Q2=makeQuery(id+"F5.boolean.opBoolean","MERGE",EDGE,{"derivedFrom":[makeQuery(id+"F1.opExtrude","CAP_EDGE",EDGE,{"disambiguationData":[OSD([sQuery(id+"F0.wireOp",EDGE,"E210")])],"isStart":false})],"fromTools":[makeQuery(id+"F5.opExtrude","SWEPT_EDGE",EDGE,{"disambiguationData":[OSD([sQuery(id+"F0.wireOp",EDGE,"E2.right"),sQuery(id+"F0.wireOp",EDGE,"E24.left"),sQuery(id+"F0.wireOp",EDGE,"E25.left"),sQuery(id+"F4.wireOp",EDGE,"E223.bottom"),sQuery(id+"F4.wireOp",EDGE,"E223.right")])]})]});
            var Q3;
            Q3=makeQuery(id+"F5.boolean.opBoolean","MERGE",EDGE,{"derivedFrom":[makeQuery(id+"F1.opExtrude","CAP_EDGE",EDGE,{"disambiguationData":[OSD([sQuery(id+"F0.wireOp",EDGE,"E211")])],"isStart":false})],"fromTools":[makeQuery(id+"F5.opExtrude","SWEPT_EDGE",EDGE,{"disambiguationData":[OSD([sQuery(id+"F0.wireOp",EDGE,"E2.right"),sQuery(id+"F0.wireOp",EDGE,"E24.left"),sQuery(id+"F0.wireOp",EDGE,"E25.left"),sQuery(id+"F4.wireOp",EDGE,"E223.bottom"),sQuery(id+"F4.wireOp",EDGE,"E223.left")])]})]});
            var Q4;
            Q4=makeQuery(id+"F7.boolean.opBoolean","MERGE",EDGE,{"derivedFrom":[makeQuery(id+"F1.opExtrude","CAP_EDGE",EDGE,{"disambiguationData":[OSD([sQuery(id+"F0.wireOp",EDGE,"E215")])],"isStart":false})],"fromTools":[makeQuery(id+"F7.opExtrude","SWEPT_EDGE",EDGE,{"disambiguationData":[OSD([sQuery(id+"F0.wireOp",EDGE,"E5.bottom"),sQuery(id+"F6.wireOp",EDGE,"E228.bottom"),sQuery(id+"F6.wireOp",EDGE,"E228.right")])]})]});
            var Q5;
            Q5=makeQuery(id+"F7.boolean.opBoolean","MERGE",EDGE,{"derivedFrom":[makeQuery(id+"F1.opExtrude","CAP_EDGE",EDGE,{"disambiguationData":[OSD([sQuery(id+"F0.wireOp",EDGE,"E214")])],"isStart":false})],"fromTools":[makeQuery(id+"F7.opExtrude","SWEPT_EDGE",EDGE,{"disambiguationData":[OSD([sQuery(id+"F0.wireOp",EDGE,"E5.bottom"),sQuery(id+"F6.wireOp",EDGE,"E228.bottom"),sQuery(id+"F6.wireOp",EDGE,"E228.left")])]})]});
            chamfer(context, id + "F9", {"entities" : qUnion([Q0, Q1, Q2, Q3, Q4, Q5]), "width" : 30 * mm, "tangentPropagation" : true});
        }
    });
